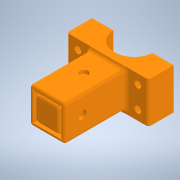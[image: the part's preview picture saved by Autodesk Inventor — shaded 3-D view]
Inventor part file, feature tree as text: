
AUTODESK INVENTOR PART (.ipt)
format: ipt  version: 2020.2 (Build 242310000, 310)  size: 354,816 bytes
history: native  units: mm
features: sketch x8, extrude x5, fillet x5, hole x3
ambient origin geometry x8: Origin, YZ Plane, XZ Plane, XY Plane, X Axis, Y Axis, Z Axis, Center Point
bodies: Solido1 (feature_tree)
feature tree (21):
  extrude  "Estrusione1"  Depth=18.0mm
  extrude  "Estrusione2"  Depth=40.0mm TaperAngle=0.0deg
  extrude  "Estrusione6"  Depth=26.0mm
  fillet  "Raccordo3"  Radius=26.0mm
  hole  "Foro8"  [1 undecoded]
  hole  "Foro9"  [1 undecoded]
  extrude  "Estrusione7"  Depth=3.0mm
  extrude  "Estrusione8"  Depth=21.0mm
  hole  "Foro10"  [1 undecoded]
  fillet  "Raccordo5"  Radius=40.0mm
  fillet  "Raccordo6"  Radius=2.0mm
  fillet  "Raccordo7"  Radius=13.0mm
  fillet  "Raccordo8"  [1 undecoded]
  sketch  "Schizzo1"
  sketch  "Schizzo2"
  sketch  "Schizzo12"
  sketch  "Schizzo13"
  sketch  "Schizzo14"
  sketch  "Schizzo17"
  sketch  "Schizzo18"
  sketch  "Schizzo19"
note: 4 required parameter values undecoded (feature->parameter linkage not recoverable at this tier; creation-order binding heuristic only, values carry confidence <= 0.55)
